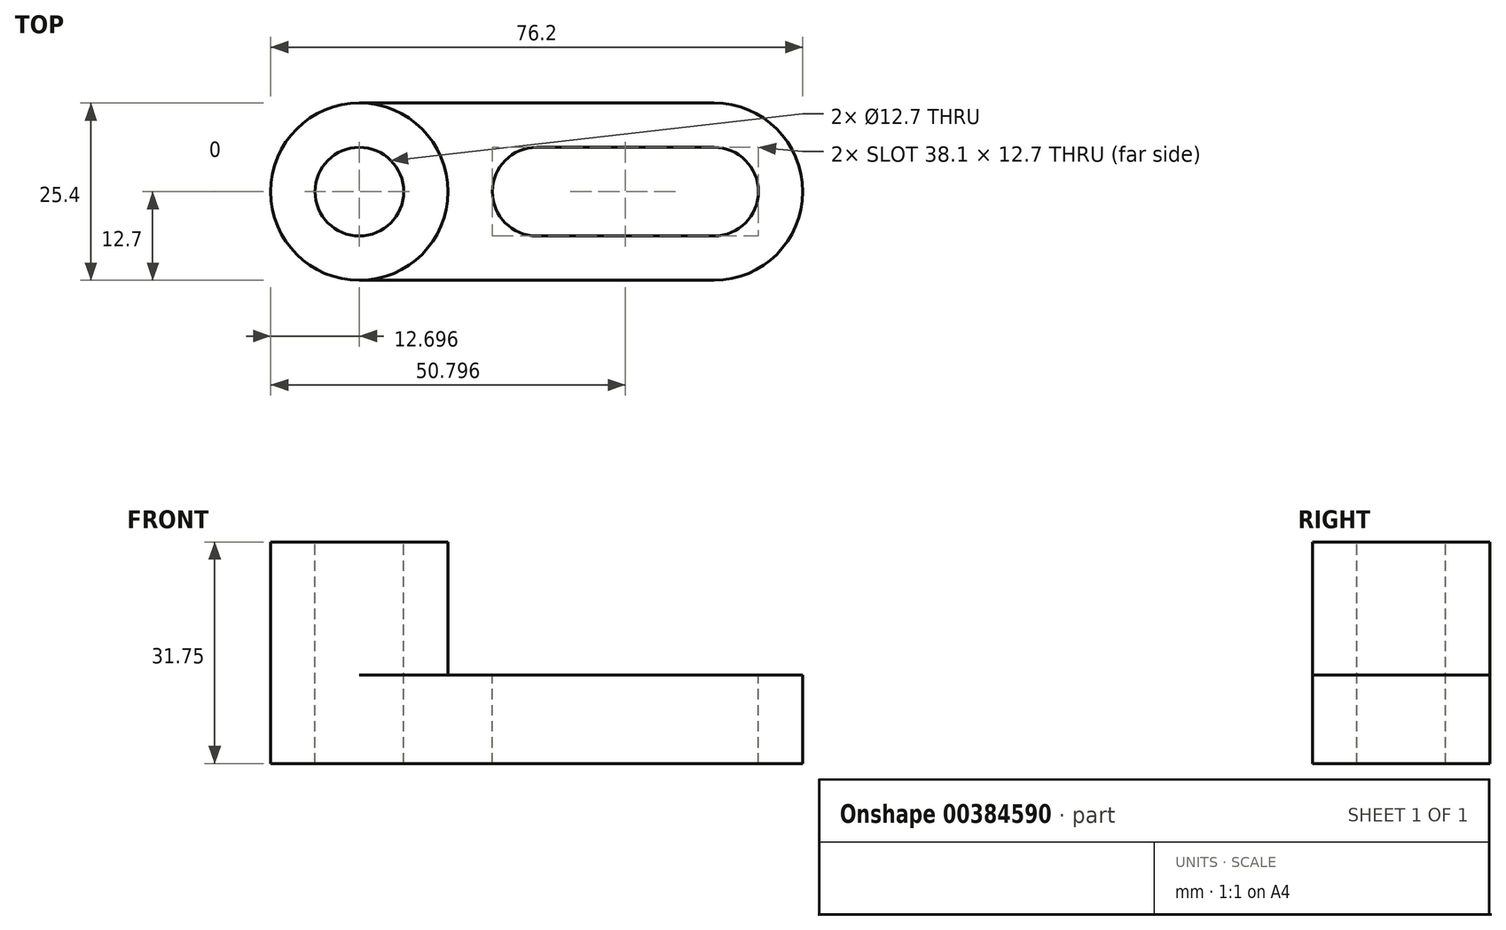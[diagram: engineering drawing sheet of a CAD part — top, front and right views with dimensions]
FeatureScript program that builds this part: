
annotation { "Feature Type Name" : "Feature", "Feature Type Description" : "" }
export const myFeature = defineFeature(function(context is Context, id is Id, definition is map)
    precondition{}
    {
        {
            var Q0;
            Q0=qCreatedBy(makeId("Front.planeOp"),FACE);
            var sketch = newSketch(context, id + "F0", { "sketchPlane" : qUnion([Q0])});
            skLineSegment(sketch, "E0", {"start": v(-61.75, 31.75) * mm, "end": v(-61.75, 0) * mm});
            skLineSegment(sketch, "E1", {"start": v(-61.75, 0) * mm, "end": v(14.45, 0) * mm});
            skLineSegment(sketch, "E2", {"start": v(14.45, 0) * mm, "end": v(14.45, 12.7) * mm});
            skLineSegment(sketch, "E3", {"start": v(14.45, 12.7) * mm, "end": v(-36.35, 12.7) * mm});
            skLineSegment(sketch, "E4", {"start": v(-61.75, 31.75) * mm, "end": v(-36.35, 31.75) * mm});
            skLineSegment(sketch, "E5", {"start": v(-36.35, 31.75) * mm, "end": v(-36.35, 12.7) * mm});
            skSolve(sketch);
        }
        {
            var Q0;
            Q0=makeQuery(id+"F0.imprint","IMPRINT",FACE,{"disambiguationData":[TD([[makeQuery(id+"F0.imprint","IMPRINT",EDGE,{"derivedFrom":sQuery(id+"F0.wireOp",EDGE,"E0")}),1.0]])]});
            extrude(context, id + "F1", {"entities" : qUnion([Q0]), "depth" : 25.4 * mm});
        }
        {
            var Q0;
            Q0=makeQuery(id+"F1.opExtrude","SWEPT_FACE",FACE,{"disambiguationData":[OSD([sQuery(id+"F0.wireOp",EDGE,"E4")])]});
            var sketch = newSketch(context, id + "F2", { "sketchPlane" : qUnion([Q0])});
            skCircle(sketch, "E6", {"center": v(-49.05, -12.7) * mm, "radius": 6.35 * mm});
            skPoint(sketch, "E6.centerSnap0", {"position": v(-61.75, -12.7) * mm});
            skSolve(sketch);
        }
        {
            var Q0;
            Q0=makeQuery(id+"F2.imprint","IMPRINT",FACE,{"disambiguationData":[TD([[makeQuery(id+"F2.imprint","IMPRINT",EDGE,{"derivedFrom":sQuery(id+"F2.wireOp",EDGE,"E6")}),1.0]])]});
            extrude(context, id + "F3", {"entities" : qUnion([Q0]), "operationType" : NewBodyOperationType.REMOVE, "oppositeDirection" : true, "depth" : 57.15 * mm});
        }
        {
            var Q0;
            Q0=makeQuery(id+"F1.opExtrude","SWEPT_FACE",FACE,{"disambiguationData":[OSD([sQuery(id+"F0.wireOp",EDGE,"E4")])]});
            var sketch = newSketch(context, id + "F4", { "sketchPlane" : qUnion([Q0])});
            skCircle(sketch, "E7", {"center": v(-49.05, -12.7) * mm, "radius": 12.7 * mm});
            skSolve(sketch);
        }
        {
            var Q0;
            {var subQ0=sQuery(id+"F4.wireOp",EDGE,"E7");var subQ1=sQuery(id+"F0.wireOp",EDGE,"E4");var subQ2=makeQuery(id+"F1.opExtrude","CAP_EDGE",EDGE,{"disambiguationData":[OSD([subQ1])],"isStart":true});var subQ3=makeQuery(id+"F4.imprint","INTERSECT",VERTEX,{"derivedFrom":[subQ2,subQ0]});Q0=makeQuery(id+"F4.imprint","IMPRINT",FACE,{"disambiguationData":[TD([[makeQuery(id+"F4.imprint","IMPRINT",EDGE,{"disambiguationData":[TD([[subQ3,-1.0]])],"derivedFrom":subQ0}),-1.0]])]});}
            var Q1;
            {var subQ0=sQuery(id+"F4.wireOp",EDGE,"E7");var subQ1=sQuery(id+"F0.wireOp",EDGE,"E4");var subQ4=makeQuery(id+"F1.opExtrude","CAP_EDGE",EDGE,{"disambiguationData":[OSD([subQ1])],"isStart":false});var subQ5=makeQuery(id+"F4.imprint","INTERSECT",VERTEX,{"derivedFrom":[subQ4,subQ0]});Q1=makeQuery(id+"F4.imprint","IMPRINT",FACE,{"disambiguationData":[TD([[makeQuery(id+"F4.imprint","IMPRINT",EDGE,{"disambiguationData":[TD([[subQ5,1.0]])],"derivedFrom":subQ0}),-1.0]])]});}
            extrude(context, id + "F5", {"entities" : qUnion([Q0, Q1]), "operationType" : NewBodyOperationType.REMOVE, "oppositeDirection" : true, "depth" : 31.75 * mm});
        }
        {
            var Q0;
            Q0=makeQuery(id+"F1.opExtrude","SWEPT_FACE",FACE,{"disambiguationData":[OSD([sQuery(id+"F0.wireOp",EDGE,"E4")])]});
            var sketch = newSketch(context, id + "F6", { "sketchPlane" : qUnion([Q0])});
            skCircle(sketch, "E8", {"center": v(-49.05, -12.7) * mm, "radius": 12.7 * mm});
            skSolve(sketch);
        }
        {
            var Q0;
            {var subQ1=sQuery(id+"F0.wireOp",EDGE,"E4");var subQ2=makeQuery(id+"F1.opExtrude","CAP_EDGE",EDGE,{"disambiguationData":[OSD([subQ1])],"isStart":true});Q0=makeQuery(id+"F6.imprint","IMPRINT",FACE,{"disambiguationData":[TD([[makeQuery(id+"F6.imprint","IMPRINT",EDGE,{"derivedFrom":subQ2}),-1.0]])]});}
            var Q1;
            {var subQ1=sQuery(id+"F0.wireOp",EDGE,"E4");var subQ2=makeQuery(id+"F1.opExtrude","CAP_EDGE",EDGE,{"disambiguationData":[OSD([subQ1])],"isStart":false});Q1=makeQuery(id+"F6.imprint","IMPRINT",FACE,{"disambiguationData":[TD([[makeQuery(id+"F6.imprint","IMPRINT",EDGE,{"derivedFrom":subQ2}),1.0]])]});}
            extrude(context, id + "F7", {"entities" : qUnion([Q0, Q1]), "operationType" : NewBodyOperationType.REMOVE, "oppositeDirection" : true, "depth" : 19.05 * mm});
        }
        {
            var Q0;
            {var subQ0=sQuery(id+"F0.wireOp",EDGE,"E4");var subQ1=makeQuery(id+"F1.opExtrude","CAP_EDGE",EDGE,{"disambiguationData":[OSD([subQ0])],"isStart":false});var subQ2=sQuery(id+"F0.wireOp",EDGE,"E5");var subQ3=makeQuery(id+"F1.opExtrude","SWEPT_EDGE",EDGE,{"disambiguationData":[OSD([subQ0,subQ2])]});var subQ4=sQuery(id+"F6.wireOp",EDGE,"E8");var subQ6=makeQuery(id+"F1.opExtrude","CAP_EDGE",EDGE,{"disambiguationData":[OSD([subQ0])],"isStart":true});Q0=makeQuery(id+"F7.boolean.opBoolean","MERGE",FACE,{"derivedFrom":[makeQuery(id+"F1.opExtrude","SWEPT_FACE",FACE,{"disambiguationData":[OSD([sQuery(id+"F0.wireOp",EDGE,"E3")])]}),makeQuery(id+"F7.opExtrude","CAP_FACE",FACE,{"disambiguationData":[OSD([subQ0,subQ2,subQ4]),TDD([makeQuery(id+"F6.imprint","IMPRINT",EDGE,{"disambiguationData":[TD([[makeQuery(id+"F6.imprint","INTERSECT",VERTEX,{"derivedFrom":[subQ6,subQ4]}),1.0]])],"derivedFrom":subQ4}),makeQuery(id+"F6.imprint","IMPRINT",EDGE,{"derivedFrom":subQ6}),makeQuery(id+"F6.imprint","IMPRINT",EDGE,{"disambiguationData":[TD([[makeQuery(id+"F6.imprint","INTERSECT",VERTEX,{"derivedFrom":[subQ3,subQ6]}),1.0]])],"derivedFrom":subQ3})])],"isStart":false}),makeQuery(id+"F7.opExtrude","CAP_FACE",FACE,{"disambiguationData":[OSD([subQ0,subQ2,subQ4]),TDD([makeQuery(id+"F6.imprint","IMPRINT",EDGE,{"disambiguationData":[TD([[makeQuery(id+"F6.imprint","INTERSECT",VERTEX,{"derivedFrom":[subQ1,subQ4]}),-1.0]])],"derivedFrom":subQ4}),makeQuery(id+"F6.imprint","IMPRINT",EDGE,{"derivedFrom":subQ1}),makeQuery(id+"F6.imprint","IMPRINT",EDGE,{"disambiguationData":[TD([[makeQuery(id+"F6.imprint","INTERSECT",VERTEX,{"derivedFrom":[subQ3,subQ1]}),-1.0]])],"derivedFrom":subQ3})])],"isStart":false})]});}
            var sketch = newSketch(context, id + "F8", { "sketchPlane" : qUnion([Q0])});
            skCircle(sketch, "E9", {"center": v(-23.65, -12.7) * mm, "radius": 6.35 * mm});
            skCircle(sketch, "E10", {"center": v(1.75, -12.7) * mm, "radius": 6.35 * mm});
            skLineSegment(sketch, "E11", {"start": v(-23.65, -6.35) * mm, "end": v(1.75, -6.35) * mm});
            skLineSegment(sketch, "E12", {"start": v(-23.65, -19.05) * mm, "end": v(1.75, -19.05) * mm});
            skSolve(sketch);
        }
        {
            var Q0;
            {var subQ0=sQuery(id+"F8.wireOp",EDGE,"E9");var subQ1=makeQuery(id+"F8.imprint","INTERSECT",VERTEX,{"derivedFrom":[subQ0,sQuery(id+"F8.wireOp",EDGE,"E11")]});Q0=makeQuery(id+"F8.imprint","IMPRINT",FACE,{"disambiguationData":[TD([[makeQuery(id+"F8.imprint","IMPRINT",EDGE,{"disambiguationData":[TD([[subQ1,-1.0]])],"derivedFrom":subQ0}),1.0]])]});}
            var Q1;
            {var subQ0=sQuery(id+"F8.wireOp",EDGE,"E11");Q1=makeQuery(id+"F8.imprint","IMPRINT",FACE,{"disambiguationData":[TD([[makeQuery(id+"F8.imprint","IMPRINT",EDGE,{"derivedFrom":subQ0}),-1.0]])]});}
            var Q2;
            {var subQ0=sQuery(id+"F8.wireOp",EDGE,"E10");var subQ1=makeQuery(id+"F8.imprint","INTERSECT",VERTEX,{"derivedFrom":[subQ0,sQuery(id+"F8.wireOp",EDGE,"E11")]});Q2=makeQuery(id+"F8.imprint","IMPRINT",FACE,{"disambiguationData":[TD([[makeQuery(id+"F8.imprint","IMPRINT",EDGE,{"disambiguationData":[TD([[subQ1,-1.0]])],"derivedFrom":subQ0}),1.0]])]});}
            extrude(context, id + "F9", {"entities" : qUnion([Q0, Q1, Q2]), "operationType" : NewBodyOperationType.REMOVE, "oppositeDirection" : true, "depth" : 12.7 * mm});
        }
        {
            var Q0;
            {var subQ0=sQuery(id+"F0.wireOp",EDGE,"E4");var subQ1=makeQuery(id+"F1.opExtrude","CAP_EDGE",EDGE,{"disambiguationData":[OSD([subQ0])],"isStart":false});var subQ2=sQuery(id+"F0.wireOp",EDGE,"E5");var subQ3=makeQuery(id+"F1.opExtrude","SWEPT_EDGE",EDGE,{"disambiguationData":[OSD([subQ0,subQ2])]});var subQ4=sQuery(id+"F6.wireOp",EDGE,"E8");var subQ6=makeQuery(id+"F1.opExtrude","CAP_EDGE",EDGE,{"disambiguationData":[OSD([subQ0])],"isStart":true});Q0=makeQuery(id+"F7.boolean.opBoolean","MERGE",FACE,{"derivedFrom":[makeQuery(id+"F1.opExtrude","SWEPT_FACE",FACE,{"disambiguationData":[OSD([sQuery(id+"F0.wireOp",EDGE,"E3")])]}),makeQuery(id+"F7.opExtrude","CAP_FACE",FACE,{"disambiguationData":[OSD([subQ0,subQ2,subQ4]),TDD([makeQuery(id+"F6.imprint","IMPRINT",EDGE,{"disambiguationData":[TD([[makeQuery(id+"F6.imprint","INTERSECT",VERTEX,{"derivedFrom":[subQ6,subQ4]}),1.0]])],"derivedFrom":subQ4}),makeQuery(id+"F6.imprint","IMPRINT",EDGE,{"derivedFrom":subQ6}),makeQuery(id+"F6.imprint","IMPRINT",EDGE,{"disambiguationData":[TD([[makeQuery(id+"F6.imprint","INTERSECT",VERTEX,{"derivedFrom":[subQ3,subQ6]}),1.0]])],"derivedFrom":subQ3})])],"isStart":false}),makeQuery(id+"F7.opExtrude","CAP_FACE",FACE,{"disambiguationData":[OSD([subQ0,subQ2,subQ4]),TDD([makeQuery(id+"F6.imprint","IMPRINT",EDGE,{"disambiguationData":[TD([[makeQuery(id+"F6.imprint","INTERSECT",VERTEX,{"derivedFrom":[subQ1,subQ4]}),-1.0]])],"derivedFrom":subQ4}),makeQuery(id+"F6.imprint","IMPRINT",EDGE,{"derivedFrom":subQ1}),makeQuery(id+"F6.imprint","IMPRINT",EDGE,{"disambiguationData":[TD([[makeQuery(id+"F6.imprint","INTERSECT",VERTEX,{"derivedFrom":[subQ3,subQ1]}),-1.0]])],"derivedFrom":subQ3})])],"isStart":false})]});}
            var sketch = newSketch(context, id + "F10", { "sketchPlane" : qUnion([Q0])});
            skArc(sketch, "E13", {"start": v(14.45, -12.7) * mm, "mid": v(10.73, -3.72) * mm, "end": v(1.75, 0) * mm});
            skArc(sketch, "E14", {"start": v(1.75, -25.4) * mm, "mid": v(10.73, -21.68) * mm, "end": v(14.45, -12.7) * mm});
            skSolve(sketch);
        }
        {
            var Q0;
            {var subQ0=sQuery(id+"F10.wireOp",EDGE,"E13");Q0=makeQuery(id+"F10.imprint","IMPRINT",FACE,{"disambiguationData":[TD([[makeQuery(id+"F10.imprint","IMPRINT",EDGE,{"derivedFrom":subQ0}),-1.0]])]});}
            var Q1;
            {var subQ0=sQuery(id+"F10.wireOp",EDGE,"E14");Q1=makeQuery(id+"F10.imprint","IMPRINT",FACE,{"disambiguationData":[TD([[makeQuery(id+"F10.imprint","IMPRINT",EDGE,{"derivedFrom":subQ0}),-1.0]])]});}
            extrude(context, id + "F11", {"entities" : qUnion([Q0, Q1]), "operationType" : NewBodyOperationType.REMOVE, "oppositeDirection" : true, "depth" : 12.7 * mm});
        }
    });
